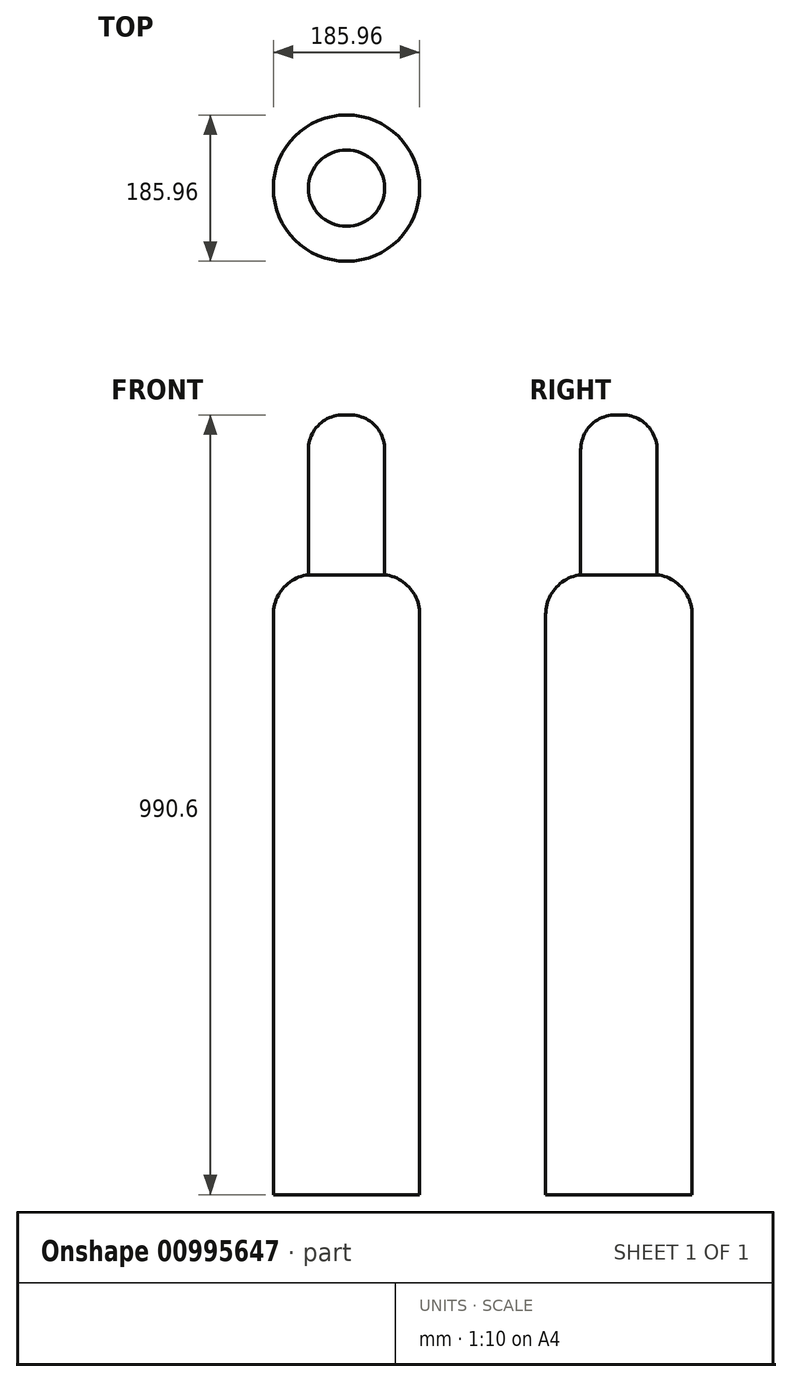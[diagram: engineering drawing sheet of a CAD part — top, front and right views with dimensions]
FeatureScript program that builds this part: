
annotation { "Feature Type Name" : "Feature", "Feature Type Description" : "" }
export const myFeature = defineFeature(function(context is Context, id is Id, definition is map)
    precondition{}
    {
        {
            var Q0;
            Q0=qCreatedBy(makeId("Top.planeOp"),FACE);
            var sketch = newSketch(context, id + "F0", { "sketchPlane" : qUnion([Q0])});
            skCircle(sketch, "E0", {"center": v(0, 0) * mm, "radius": 92.98 * mm});
            skSolve(sketch);
        }
        {
            var Q0;
            Q0=makeQuery(id+"F0.imprint","IMPRINT",FACE,{"disambiguationData":[TD([[makeQuery(id+"F0.imprint","IMPRINT",EDGE,{"derivedFrom":sQuery(id+"F0.wireOp",EDGE,"E0")}),1.0]])]});
            extrude(context, id + "F1", {"entities" : qUnion([Q0]), "depth" : 787.4 * mm, "offsetDistance" : 25.4 * mm});
        }
        {
            var Q0;
            Q0=makeQuery(id+"F1.opExtrude","CAP_FACE",FACE,{"disambiguationData":[OSD([sQuery(id+"F0.wireOp",EDGE,"E0")])],"isStart":false});
            var sketch = newSketch(context, id + "F2", { "sketchPlane" : qUnion([Q0])});
            skCircle(sketch, "E1", {"center": v(0, 0) * mm, "radius": 48.51 * mm});
            skSolve(sketch);
        }
        {
            var Q0;
            Q0 = qSketchRegion(id + "F2", true);
            extrude(context, id + "F3", {"entities" : qUnion([Q0]), "operationType" : NewBodyOperationType.ADD, "depth" : 203.2 * mm, "offsetDistance" : 25.4 * mm});
        }
        {
            var Q0;
            Q0=makeQuery(id+"F3.opExtrude","CAP_EDGE",EDGE,{"disambiguationData":[OSD([sQuery(id+"F2.wireOp",EDGE,"E1")])],"isStart":false});
            fillet(context, id + "F4", {"entities" : qUnion([Q0]), "radius" : 44.45 * mm, "tangentPropagation" : true, "allowEdgeOverflow" : false});
        }
        {
            var Q0;
            Q0=makeQuery(id+"F1.opExtrude","CAP_EDGE",EDGE,{"disambiguationData":[OSD([sQuery(id+"F0.wireOp",EDGE,"E0")])],"isStart":false});
            fillet(context, id + "F5", {"entities" : qUnion([Q0]), "radius" : 50.8 * mm, "tangentPropagation" : true, "allowEdgeOverflow" : false});
        }
    });
